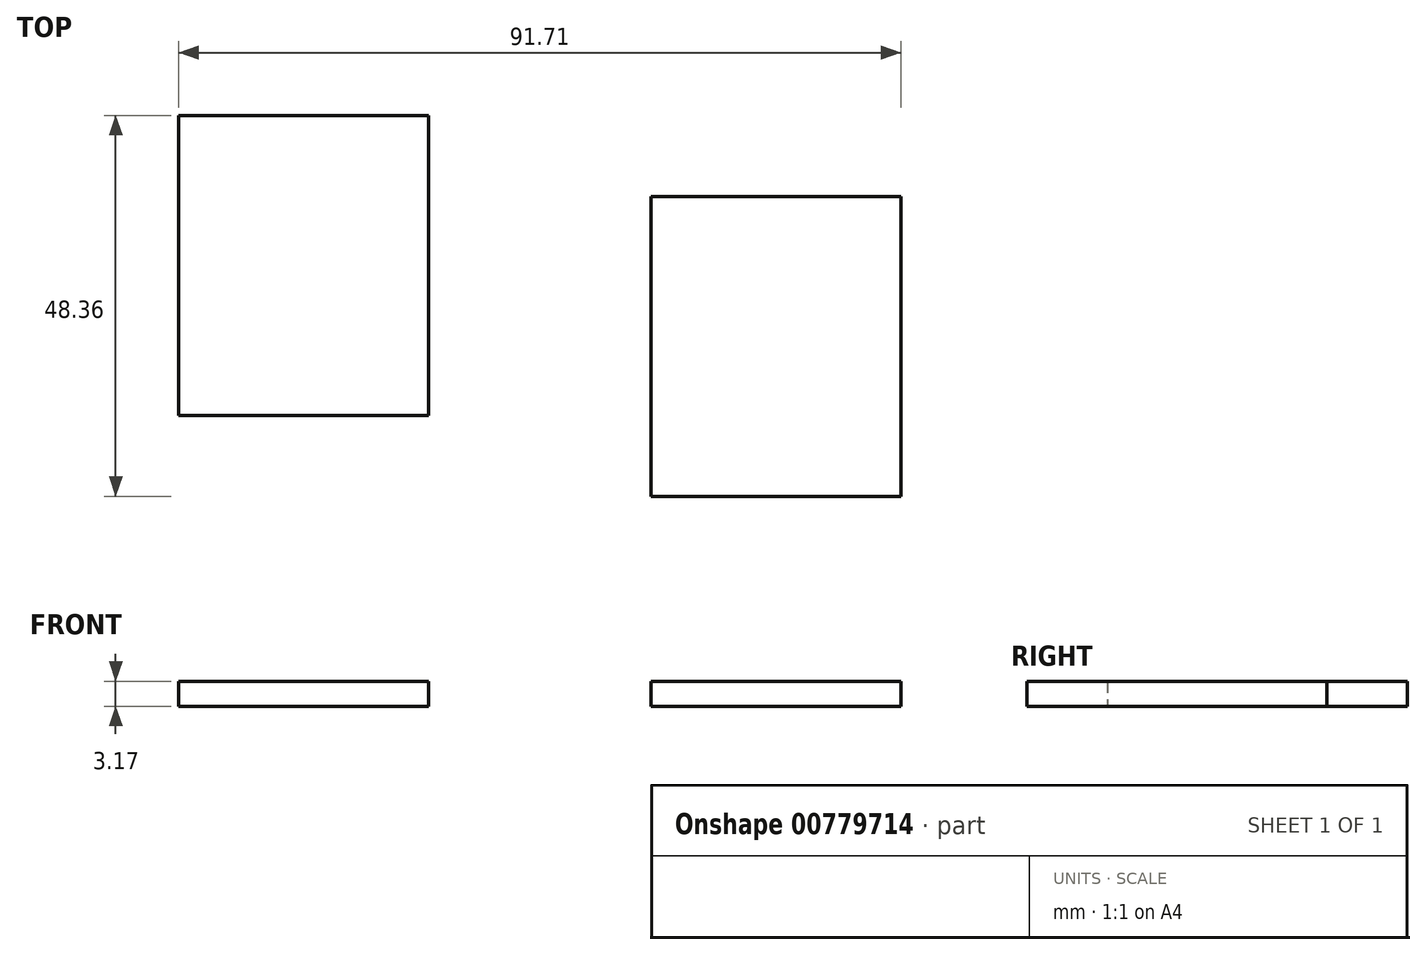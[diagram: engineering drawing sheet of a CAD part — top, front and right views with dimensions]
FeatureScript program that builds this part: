
annotation { "Feature Type Name" : "Feature", "Feature Type Description" : "" }
export const myFeature = defineFeature(function(context is Context, id is Id, definition is map)
    precondition{}
    {
        {
            var Q0;
            Q0=qCreatedBy(makeId("Top.planeOp"),FACE);
            var sketch = newSketch(context, id + "F0", { "sketchPlane" : qUnion([Q0])});
            skLineSegment(sketch, "E0.bottom", {"start": v(-10.58, 27.84) * mm, "end": v(21.17, 27.84) * mm});
            skLineSegment(sketch, "E0.top", {"start": v(-10.58, -10.26) * mm, "end": v(21.17, -10.26) * mm});
            skLineSegment(sketch, "E0.left", {"start": v(-10.58, 27.84) * mm, "end": v(-10.58, -10.26) * mm});
            skLineSegment(sketch, "E0.right", {"start": v(21.17, 27.84) * mm, "end": v(21.17, -10.26) * mm});
            skLineSegment(sketch, "E1.bottom", {"start": v(-70.54, 38.1) * mm, "end": v(-38.79, 38.1) * mm});
            skLineSegment(sketch, "E1.top", {"start": v(-70.54, 0) * mm, "end": v(-38.79, 0) * mm});
            skLineSegment(sketch, "E1.left", {"start": v(-70.54, 38.1) * mm, "end": v(-70.54, 0) * mm});
            skLineSegment(sketch, "E1.right", {"start": v(-38.79, 38.1) * mm, "end": v(-38.79, 0) * mm});
            skSolve(sketch);
        }
        {
            var Q0;
            Q0 = qSketchRegion(id + "F0", true);
            extrude(context, id + "F1", {"entities" : qUnion([Q0]), "depth" : 3.17 * mm, "offsetDistance" : 25.4 * mm});
        }
    });
